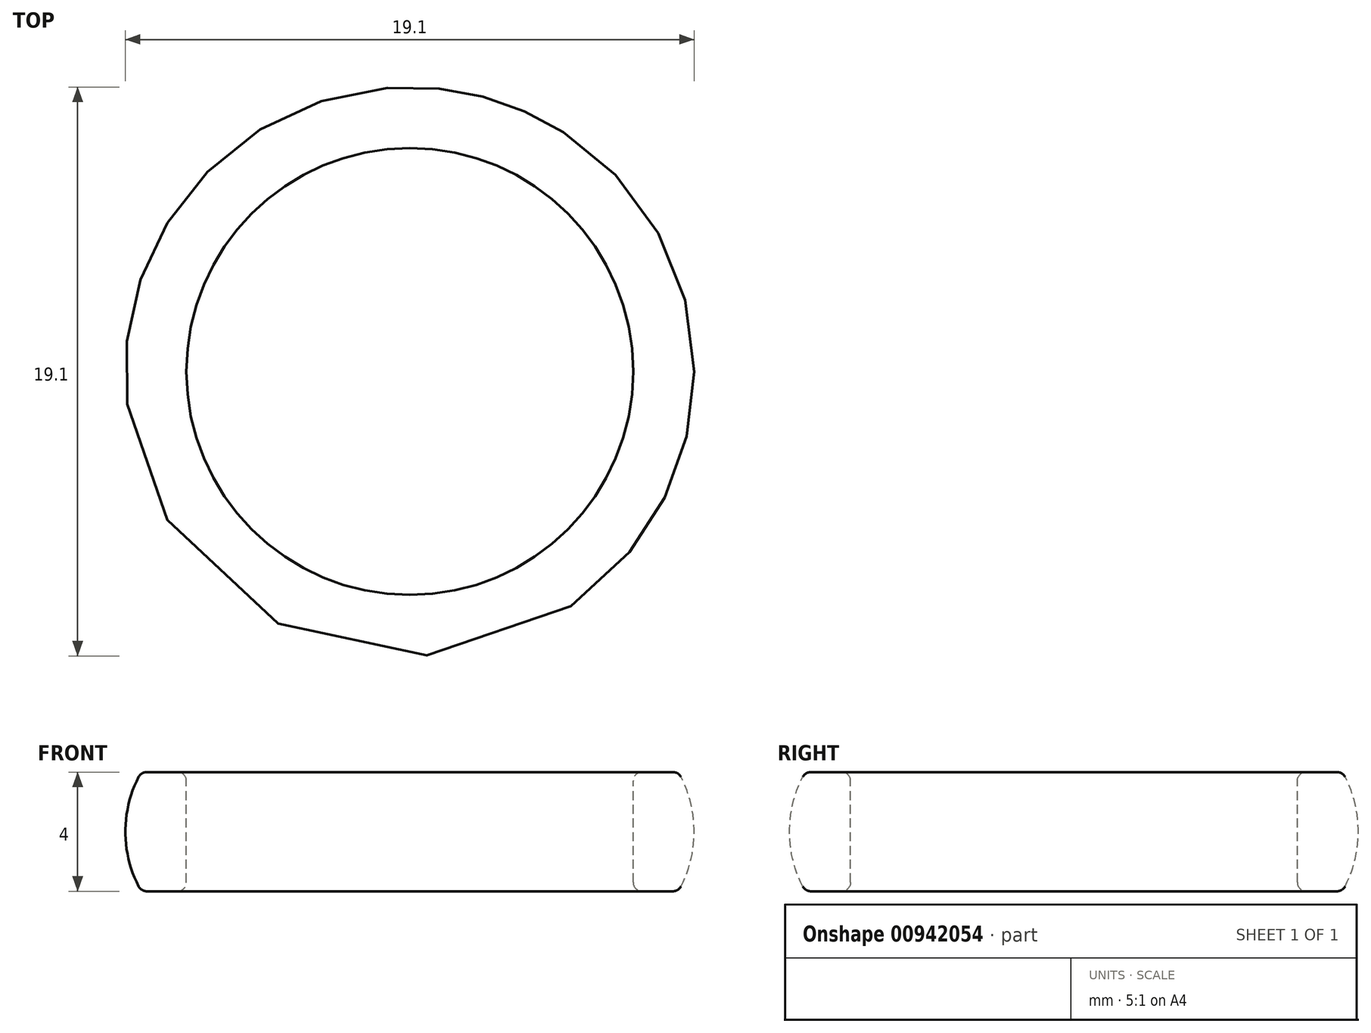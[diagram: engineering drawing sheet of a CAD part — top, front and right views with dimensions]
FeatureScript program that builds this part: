
annotation { "Feature Type Name" : "Feature", "Feature Type Description" : "" }
export const myFeature = defineFeature(function(context is Context, id is Id, definition is map)
    precondition{}
    {
        {
            var Q0;
            Q0=qCreatedBy(makeId("Top.planeOp"),FACE);
            var sketch = newSketch(context, id + "F0", { "sketchPlane" : qUnion([Q0])});
            skCircle(sketch, "E0", {"center": v(0, 0) * mm, "radius": 7.5 * mm});
            skLineSegment(sketch, "E1", {"start": v(0, 0) * mm, "end": v(7.5, 0) * mm});
            skSolve(sketch);
        }
        {
            var Q0;
            Q0=qCreatedBy(makeId("Front.planeOp"),FACE);
            var sketch = newSketch(context, id + "F1", { "sketchPlane" : qUnion([Q0])});
            skLineSegment(sketch, "E2", {"start": v(7.5, 0) * mm, "end": v(7.5, 4) * mm});
            skLineSegment(sketch, "E3", {"start": v(7.5, 0) * mm, "end": v(9.01, 0) * mm});
            skLineSegment(sketch, "E4", {"start": v(7.5, 4) * mm, "end": v(9.01, 4) * mm});
            skArc(sketch, "E5", {"start": v(9.01, 0) * mm, "mid": v(9.55, 2) * mm, "end": v(9.01, 4) * mm});
            skSolve(sketch);
        }
        {
            var Q0;
            Q0=makeQuery(id+"F1.imprint","IMPRINT",FACE,{"disambiguationData":[TD([[makeQuery(id+"F1.imprint","IMPRINT",EDGE,{"derivedFrom":sQuery(id+"F1.wireOp",EDGE,"E2")}),-1.0]])]});
            var Q1;
            Q1=sQuery(id+"F0.wireOp",EDGE,"E0");
            sweep(context, id + "F2", {"profiles" : qUnion([Q0]), "path" : qUnion([Q1])});
        }
        {
            var Q0;
            Q0=makeQuery(id+"F2.opSweep","SWEPT_EDGE",EDGE,{"disambiguationData":[OSD([sQuery(id+"F0.wireOp",EDGE,"E0"),sQuery(id+"F1.wireOp",EDGE,"E2"),sQuery(id+"F1.wireOp",EDGE,"E4")])]});
            var Q1;
            Q1=makeQuery(id+"F2.opSweep","SWEPT_EDGE",EDGE,{"disambiguationData":[OSD([sQuery(id+"F0.wireOp",EDGE,"E0"),sQuery(id+"F1.wireOp",EDGE,"E2"),sQuery(id+"F1.wireOp",EDGE,"E3")])]});
            var Q2;
            Q2=makeQuery(id+"F2.opSweep","SWEPT_EDGE",EDGE,{"disambiguationData":[OSD([sQuery(id+"F0.wireOp",EDGE,"E0"),sQuery(id+"F1.wireOp",EDGE,"E4"),sQuery(id+"F1.wireOp",EDGE,"E5")])]});
            var Q3;
            Q3=makeQuery(id+"F2.opSweep","SWEPT_EDGE",EDGE,{"disambiguationData":[OSD([sQuery(id+"F0.wireOp",EDGE,"E0"),sQuery(id+"F1.wireOp",EDGE,"E3"),sQuery(id+"F1.wireOp",EDGE,"E5")])]});
            fillet(context, id + "F3", {"entities" : qUnion([Q0, Q1, Q2, Q3]), "radius" : 0.3 * mm, "tangentPropagation" : true, "allowEdgeOverflow" : false});
        }
    });
